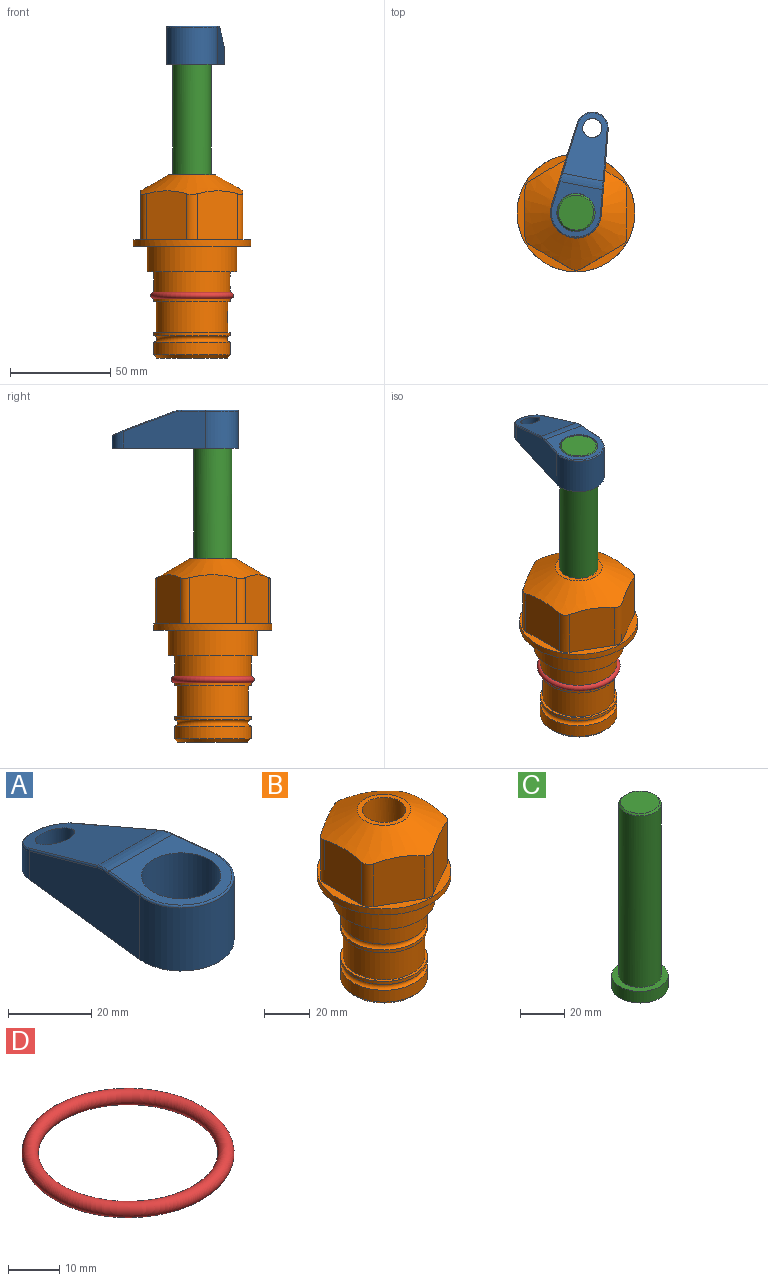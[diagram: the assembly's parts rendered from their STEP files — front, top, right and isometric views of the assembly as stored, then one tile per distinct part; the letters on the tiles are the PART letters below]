
ASSEMBLY  parts=4 mates=2
PART A: 44 faces, bbox 27.5x64.5x19.1 mm
  f0: plane 2.3x0.95mm, normal (0,0,-1), area 1mm2, adj f25,f30,f34
  f1: plane 63.5x25.4mm, normal (0,0,-1), area 561.7mm2, adj f2,f3,f4,f5,f6,f7,f19,f20
  f2: cylinder r=12.7mm len=25.4mm, axis (0,0,-1), area 792.2mm2, adj f1,f3,f5,f13
  f3: plane 42.33x18.54mm, normal (0.99,0.11,0), area 647mm2, adj f1,f2,f4,f11,f12,f14
  f4: cylinder r=7.94mm len=15.78mm, axis (0,0,-1), area 158.6mm2, adj f1,f3,f5,f16
  f5: plane 42.33x18.54mm, normal (-0.99,0.11,0), area 647mm2, adj f1,f2,f4,f15,f17,f18
  f6: cylinder r=9.53mm len=19.05mm, axis (0,0,-1), area 1140.1mm2, adj f1,f8
  f7: cylinder r=4.76mm len=10.98mm, axis (0,0,-1), area 276.1mm2, adj f1,f9
  f8: plane 25.83x24.38mm, normal (0,0,1), area 262.2mm2, adj f6,f10,f11,f13,f15
  f9: plane 32.49x20.55mm, normal (0,0.34,0.94), area 489.9mm2, adj f7,f10,f14,f16,f18
  f10: cylinder r=12.7mm len=21.49mm, axis (-1,0,0), area 93.2mm2, adj f8,f9,f12,f17
  f11: cylinder r=0.51mm len=12.34mm, axis (0.11,-0.99,0), area 9.9mm2, adj f3,f8,f12,f13
  f12: bspline ~7.62x1.64mm, area 3.5mm2, adj f3,f10,f11,f14
  f13: torus R=12.19mm, axis (0,0,1), area 33.6mm2, adj f2,f8,f11,f15
  f14: cylinder r=0.51mm len=26.01mm, axis (0.1,-0.93,0.34), area 21.6mm2, adj f3,f9,f12,f16
  f15: cylinder r=0.51mm len=12.34mm, axis (0.11,0.99,0), area 9.9mm2, adj f5,f8,f13,f17
  f16: bspline ~15.78x7.05mm, area 15.7mm2, adj f4,f9,f14,f18
  f17: bspline ~7.62x1.64mm, area 3.5mm2, adj f5,f10,f15,f18
  f18: cylinder r=0.51mm len=26.01mm, axis (0.1,0.93,-0.34), area 21.6mm2, adj f5,f9,f16,f17
  f19: plane 21.6x14.29mm, normal (-0.99,-0.11,0), area 242.6mm2, adj f1,f26,f28,f34,f36,f38
  f20: plane 21.6x14.29mm, normal (0.99,-0.11,0), area 242.6mm2, adj f1,f27,f29,f37,f39,f41
  f21: cylinder r=12.7mm len=14.29mm, axis (0,0,-1), area 173.2mm2, adj f1,f26,f27,f30,f31,f33
  f22: cylinder r=7.94mm len=7.63mm, axis (0,0,-1), area 53.8mm2, adj f1,f28,f29,f42
  f23: plane 2.3x0.95mm, normal (0,0,-1), area 1mm2, adj f25,f33,f37
  f24: plane 17.94x12.32mm, normal (0,-0.34,-0.94), area 191.2mm2, adj f25,f38,f41,f42
  f25: cylinder r=9.53mm len=12.93mm, axis (-1,0,0), area 37.5mm2, adj f0,f23,f24,f31,f36,f39
  f26: cylinder r=1.59mm len=14.29mm, axis (0,0,-1), area 49mm2, adj f1,f19,f21,f32
  f27: cylinder r=1.59mm len=14.29mm, axis (0,0,-1), area 49mm2, adj f1,f20,f21,f35
  f28: cylinder r=1.59mm len=7.28mm, axis (0,0,-1), area 22.1mm2, adj f1,f19,f22,f40
  f29: cylinder r=1.59mm len=7.28mm, axis (0,0,-1), area 22.1mm2, adj f1,f20,f22,f43
  f30: torus R=14.29mm, axis (0,0,1), area 5.8mm2, adj f0,f21,f31,f32
  f31: bspline ~11.06x2.73mm, area 20.8mm2, adj f21,f25,f30,f33
  f32: sphere r=1.59mm, area 5.4mm2, adj f26,f30,f34
  f33: torus R=14.29mm, axis (0,0,1), area 5.8mm2, adj f21,f23,f31,f35
  f34: cylinder r=1.59mm len=1.68mm, axis (-0.11,0.99,0), area 2.4mm2, adj f0,f19,f32,f36
  f35: sphere r=1.59mm, area 5.4mm2, adj f27,f33,f37
  f36: bspline ~5.82x2.33mm, area 7.7mm2, adj f19,f25,f34,f38
  f37: cylinder r=1.59mm len=1.68mm, axis (0.11,0.99,0), area 2.4mm2, adj f20,f23,f35,f39
  f38: cylinder r=1.59mm len=18.33mm, axis (0.1,-0.93,0.34), area 46.7mm2, adj f19,f24,f36,f40
  f39: bspline ~5.82x2.33mm, area 7.7mm2, adj f20,f25,f37,f41
  f40: sphere r=1.59mm, area 3.6mm2, adj f28,f38,f42
  f41: cylinder r=1.59mm len=18.33mm, axis (0.1,0.93,-0.34), area 46.7mm2, adj f20,f24,f39,f43
  f42: bspline ~8.31x1.84mm, area 15.3mm2, adj f22,f24,f40,f43
  f43: sphere r=1.59mm, area 3.6mm2, adj f29,f41,f42
PART B: 36 faces, bbox 58.7x58.7x91.2 mm
  f0: cylinder r=17.78mm len=35.56mm, axis (0,0,1), area 1670.8mm2, adj f23,f24,f31
  f1: cylinder r=19.05mm len=38.1mm, axis (0,0,1), area 1191.9mm2, adj f26,f27,f30
  f2: plane 58.66x58.66mm, normal (0,0,-1), area 1150.6mm2, adj f3,f28
  f3: cylinder r=29.33mm len=58.66mm, axis (0,0,-1), area 585.1mm2, adj f2,f4
  f4: plane 58.66x58.66mm, normal (0,0,1), area 475.9mm2, adj f3,f5,f6,f7,f8,f9,f10,f11
  f5: plane 24.5x20.32mm, normal (-0.5,0.87,0), area 562.8mm2, adj f4,f15,f16,f17
  f6: plane 24.5x20.32mm, normal (0.5,0.87,0), area 562.8mm2, adj f4,f14,f15,f17
  f7: plane 24.5x23.48mm, normal (1,0,0), area 562.8mm2, adj f4,f13,f14,f17
  f8: plane 24.5x20.32mm, normal (0.5,-0.87,0), area 562.8mm2, adj f4,f12,f13,f17
  f9: plane 24.5x20.32mm, normal (-0.5,-0.87,0), area 562.8mm2, adj f4,f11,f12,f17
  f10: plane 24.5x23.48mm, normal (-1,0,0), area 562.8mm2, adj f4,f11,f16,f17
  f11: cylinder r=5.08mm len=23.01mm, axis (0,0,-1), area 121.2mm2, adj f4,f9,f10,f17
  f12: cylinder r=5.08mm len=23.01mm, axis (0,0,-1), area 121.2mm2, adj f4,f8,f9,f17
  f13: cylinder r=5.08mm len=23.01mm, axis (0,0,-1), area 121.2mm2, adj f4,f7,f8,f17
  f14: cylinder r=5.08mm len=23.01mm, axis (0,0,-1), area 121.2mm2, adj f4,f6,f7,f17
  f15: cylinder r=5.08mm len=23.01mm, axis (0,0,-1), area 121.2mm2, adj f4,f5,f6,f17
  f16: cylinder r=5.08mm len=23.01mm, axis (0,0,-1), area 121.2mm2, adj f4,f5,f10,f17
  f17: cone r=11.73mm half-angle=60deg, axis (0,0,-1), area 2071.8mm2, adj f5,f6,f7,f8,f9,f10,f11,f12
  f18: plane 23.46x23.46mm, normal (0,0,1), area 147.4mm2, adj f17,f35
  f19: plane 34.93x34.93mm, normal (0,0,-1), area 958mm2, adj f29
  f20: cylinder r=19.05mm len=38.1mm, axis (0,0,1), area 760.1mm2, adj f21,f29
  f21: torus R=19.05mm, axis (0,0,1), area 565.3mm2, adj f20,f22
  f22: cylinder r=19.05mm len=38.1mm, axis (0,0,1), area 190mm2, adj f21,f23
  f23: plane 38.1x38.1mm, normal (0,0,1), area 146.9mm2, adj f0,f22
  f24: plane 38.1x38.1mm, normal (0,0,-1), area 146.9mm2, adj f0,f25
  f25: cylinder r=19.05mm len=38.1mm, axis (0,0,1), area 190mm2, adj f24,f26
  f26: torus R=19.05mm, axis (0,0,1), area 565.3mm2, adj f1,f25
  f27: plane 44.45x44.45mm, normal (0,0,-1), area 411.7mm2, adj f1,f28
  f28: cylinder r=22.23mm len=44.45mm, axis (0,0,1), area 1773.5mm2, adj f2,f27
  f29: cone r=19.05mm half-angle=45deg, axis (0,0,1), area 257.5mm2, adj f19,f20
  f30: cylinder r=3.17mm len=6.75mm, axis (-1,0,0), area 128mm2, adj f1,f33
  f31: cylinder r=3.17mm len=6.35mm, axis (-1,0,0), area 102.5mm2, adj f0,f33
  f32: plane 25.4x25.4mm, normal (0,0,1), area 506.7mm2, adj f33
  f33: cylinder r=12.7mm len=66.42mm, axis (0,0,-1), area 5236.2mm2, adj f30,f31,f32,f34
  f34: cone r=9.53mm half-angle=30deg, axis (0,0,-1), area 443.4mm2, adj f33,f35
  f35: cylinder r=9.53mm len=19.05mm, axis (0,0,-1), area 849mm2, adj f18,f34
PART C: 6 faces, bbox 25.4x25.4x101.6 mm
  f0: plane 17.46x17.46mm, normal (0,0,1), area 239.5mm2, adj f5
  f1: plane 25.4x25.4mm, normal (0,0,-1), area 506.7mm2, adj f2
  f2: cylinder r=12.7mm len=25.4mm, axis (0,0,1), area 506.7mm2, adj f1,f3
  f3: plane 25.4x25.4mm, normal (0,0,1), area 221.7mm2, adj f2,f4
  f4: cylinder r=9.53mm len=94.46mm, axis (0,0,1), area 5653mm2, adj f3,f5
  f5: cone r=8.73mm half-angle=45deg, axis (0,0,-1), area 64.4mm2, adj f0,f4
PART D: 1 faces, bbox 44.7x44.7x3.2 mm
  f0: torus R=19.05mm, axis (0,0,1), area 1193.9mm2
PLACE A rot(axis=(0,0,-1),10.9deg) t=(0,0,90.68)mm
PLACE B at identity fixed
PLACE C rot(axis=(0,0,-1),10.9deg) t=(0,0,36.07)mm
PLACE D at identity
MATE fastened A.f2 <-> C.f2  axis (0,0,-1) through (0,0,109.73)mm
MATE cylindrical C.f2 <-> B.f0  axis (0,0,1) through (0,0,61.71)mm
